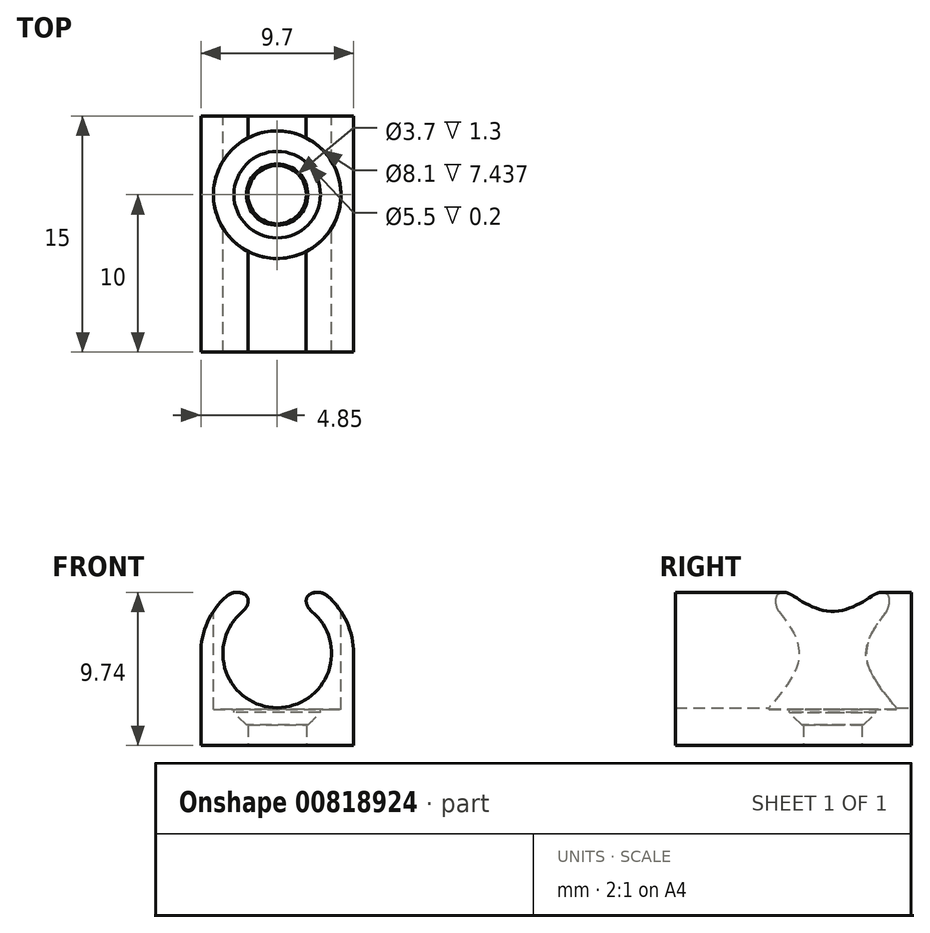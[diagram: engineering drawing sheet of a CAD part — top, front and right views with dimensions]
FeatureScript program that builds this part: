
annotation { "Feature Type Name" : "Feature", "Feature Type Description" : "" }
export const myFeature = defineFeature(function(context is Context, id is Id, definition is map)
    precondition{}
    {
        {
            var Q0;
            Q0=qCreatedBy(makeId("Front.planeOp"),FACE);
            var sketch = newSketch(context, id + "F0", { "sketchPlane" : qUnion([Q0])});
            skCircle(sketch, "E0", {"center": v(0, 0) * mm, "radius": 3.45 * mm});
            skArc(sketch, "E1.0", {"start": v(4.85, 0) * mm, "mid": v(0, 4.85) * mm, "end": v(-4.85, 0) * mm});
            skLineSegment(sketch, "E2", {"start": v(1.54, 3.09) * mm, "end": v(2.16, 4.34) * mm});
            skLineSegment(sketch, "E3.MirrorCS", {"start": v(-1.54, 3.09) * mm, "end": v(-2.16, 4.34) * mm});
            skLineSegment(sketch, "E4.bottom", {"start": v(-4.85, 0) * mm, "end": v(4.85, 0) * mm});
            skLineSegment(sketch, "E4.top", {"start": v(-4.85, -4.85) * mm, "end": v(4.85, -4.85) * mm});
            skLineSegment(sketch, "E4.left", {"start": v(-4.85, 0) * mm, "end": v(-4.85, -4.85) * mm});
            skLineSegment(sketch, "E4.right", {"start": v(4.85, 0) * mm, "end": v(4.85, -4.85) * mm});
            skLineSegment(sketch, "E5.0", {"start": v(-4.85, -5.85) * mm, "end": v(4.85, -5.85) * mm});
            skLineSegment(sketch, "E6", {"start": v(4.85, -5.85) * mm, "end": v(4.85, -4.85) * mm});
            skLineSegment(sketch, "E7", {"start": v(-4.85, -5.85) * mm, "end": v(-4.85, -4.85) * mm});
            skSolve(sketch);
        }
        {
            var Q0;
            Q0=makeQuery(id+"F0.imprint","IMPRINT",FACE,{"disambiguationData":[TD([[makeQuery(id+"F0.imprint","IMPRINT",EDGE,{"derivedFrom":sQuery(id+"F0.wireOp",EDGE,"E4.top")}),1.0]])]});
            var Q1;
            {var subQ0=sQuery(id+"F0.wireOp",EDGE,"E3.MirrorCS");Q1=makeQuery(id+"F0.imprint","IMPRINT",FACE,{"disambiguationData":[TD([[makeQuery(id+"F0.imprint","IMPRINT",EDGE,{"derivedFrom":subQ0}),1.0]])]});}
            var Q2;
            {var subQ0=sQuery(id+"F0.wireOp",EDGE,"E2");Q2=makeQuery(id+"F0.imprint","IMPRINT",FACE,{"disambiguationData":[TD([[makeQuery(id+"F0.imprint","IMPRINT",EDGE,{"derivedFrom":subQ0}),-1.0]])]});}
            var Q3;
            Q3=makeQuery(id+"F0.imprint","IMPRINT",FACE,{"disambiguationData":[TD([[makeQuery(id+"F0.imprint","IMPRINT",EDGE,{"derivedFrom":sQuery(id+"F0.wireOp",EDGE,"E4.top")}),-1.0]])]});
            extrude(context, id + "F1", {"entities" : qUnion([Q0, Q1, Q2, Q3]), "depth" : 15 * mm, "offsetDistance" : 25 * mm});
        }
        {
            var Q0;
            Q0=makeQuery(id+"F1.opExtrude","SWEPT_FACE",FACE,{"disambiguationData":[OSD([sQuery(id+"F0.wireOp",EDGE,"E5.0")])]});
            var sketch = newSketch(context, id + "F2", { "sketchPlane" : qUnion([Q0])});
            skLineSegment(sketch, "E8", {"start": v(0, 10) * mm, "end": v(0, 0) * mm, "construction": true});
            skPoint(sketch, "E9", {"position": v(0, 5) * mm});
            skCircle(sketch, "E10", {"center": v(0, 5) * mm, "radius": 1.85 * mm});
            skSolve(sketch);
        }
        {
            var Q0;
            Q0=makeQuery(id+"F2.imprint","IMPRINT",FACE,{"disambiguationData":[TD([[makeQuery(id+"F2.imprint","IMPRINT",EDGE,{"derivedFrom":sQuery(id+"F2.wireOp",EDGE,"E10")}),1.0]])]});
            extrude(context, id + "F3", {"entities" : qUnion([Q0]), "operationType" : NewBodyOperationType.REMOVE, "endBound" : BoundingType.THROUGH_ALL, "oppositeDirection" : true, "depth" : 25 * mm, "offsetDistance" : 25 * mm});
        }
        {
            var Q0;
            Q0=makeQuery(id+"F1.opExtrude","SWEPT_FACE",FACE,{"disambiguationData":[OSD([sQuery(id+"F0.wireOp",EDGE,"E5.0")])]});
            cPlane(context, id + "F4", {"entities" : qUnion([Q0]), "cplaneType" : CPlaneType.OFFSET, "offset" : 10.8 * mm, "oppositeDirection" : true, "width" : 150 * mm, "height" : 150 * mm});
        }
        {
            var Q0;
            Q0=qCreatedBy(id+"F4.planeOp",FACE);
            var sketch = newSketch(context, id + "F5", { "sketchPlane" : qUnion([Q0])});
            skLineSegment(sketch, "E11.0.0", {"start": v(-4.85, 0) * mm, "end": v(4.85, 0) * mm});
            skLineSegment(sketch, "E11.0.1", {"start": v(4.85, 0) * mm, "end": v(4.85, 15) * mm});
            skLineSegment(sketch, "E11.0.2", {"start": v(4.85, 15) * mm, "end": v(-4.85, 15) * mm});
            skLineSegment(sketch, "E11.0.3", {"start": v(-4.85, 15) * mm, "end": v(-4.85, 0) * mm});
            skCircle(sketch, "E12.0", {"center": v(0, 5) * mm, "radius": 1.85 * mm});
            skCircle(sketch, "E13", {"center": v(0, 5) * mm, "radius": 4.05 * mm});
            skSolve(sketch);
        }
        {
            var Q0;
            Q0=makeQuery(id+"F5.imprint","IMPRINT",FACE,{"disambiguationData":[TD([[makeQuery(id+"F5.imprint","IMPRINT",EDGE,{"derivedFrom":sQuery(id+"F5.wireOp",EDGE,"E12.0")}),-1.0]])]});
            var Q1;
            Q1=sQuery(id+"F5.wireOp",EDGE,"E13");
            extrude(context, id + "F6", {"entities" : qUnion([Q0]), "operationType" : NewBodyOperationType.REMOVE, "surfaceOperationType" : NewSurfaceOperationType.ADD, "surfaceEntities" : qUnion([Q1]), "depth" : 8.5 * mm, "offsetDistance" : 25 * mm});
        }
        {
            var Q0;
            Q0=makeQuery(id+"F6.boolean.opBoolean","COPY",FACE,{"derivedFrom":makeQuery(id+"F6.opExtrude","CAP_FACE",FACE,{"disambiguationData":[OSD([sQuery(id+"F5.wireOp",EDGE,"E12.0"),sQuery(id+"F5.wireOp",EDGE,"E13")])],"isStart":false})});
            var sketch = newSketch(context, id + "F7", { "sketchPlane" : qUnion([Q0])});
            skCircle(sketch, "E14.0", {"center": v(0, -5) * mm, "radius": 1.85 * mm});
            skCircle(sketch, "E15", {"center": v(0, -5) * mm, "radius": 2.75 * mm});
            skSolve(sketch);
        }
        {
            var Q0;
            Q0=makeQuery(id+"F7.imprint","IMPRINT",FACE,{"disambiguationData":[TD([[makeQuery(id+"F7.imprint","IMPRINT",EDGE,{"derivedFrom":sQuery(id+"F7.wireOp",EDGE,"E14.0")}),1.0]])]});
            extrude(context, id + "F8", {"entities" : qUnion([Q0]), "operationType" : NewBodyOperationType.REMOVE, "oppositeDirection" : true, "depth" : 1 * mm, "offsetDistance" : 25 * mm});
        }
        {
            var Q0;
            Q0=makeQuery(id+"F1.opExtrude","SWEPT_EDGE",EDGE,{"disambiguationData":[OSD([sQuery(id+"F0.wireOp",EDGE,"E1.0"),sQuery(id+"F0.wireOp",EDGE,"E3.MirrorCS")])]});
            var Q1;
            Q1=makeQuery(id+"F1.opExtrude","SWEPT_EDGE",EDGE,{"disambiguationData":[OSD([sQuery(id+"F0.wireOp",EDGE,"E0"),sQuery(id+"F0.wireOp",EDGE,"E3.MirrorCS")])]});
            var Q2;
            Q2=makeQuery(id+"F1.opExtrude","SWEPT_EDGE",EDGE,{"disambiguationData":[OSD([sQuery(id+"F0.wireOp",EDGE,"E1.0"),sQuery(id+"F0.wireOp",EDGE,"E2")])]});
            var Q3;
            Q3=makeQuery(id+"F1.opExtrude","SWEPT_EDGE",EDGE,{"disambiguationData":[OSD([sQuery(id+"F0.wireOp",EDGE,"E0"),sQuery(id+"F0.wireOp",EDGE,"E2")])]});
            fillet(context, id + "F9", {"entities" : qUnion([Q0, Q1, Q2, Q3]), "radius" : 1 * mm, "tangentPropagation" : true, "allowEdgeOverflow" : false});
        }
        {
            var Q0;
            {var subQ0=sQuery(id+"F0.wireOp",EDGE,"E3.MirrorCS");Q0=makeQuery(id+"F9.opFillet","BLEND_EDGE",EDGE,{"blendedFrom":[makeQuery(id+"F1.opExtrude","SWEPT_EDGE",EDGE,{"disambiguationData":[OSD([sQuery(id+"F0.wireOp",EDGE,"E0"),subQ0])]}),makeQuery(id+"F1.opExtrude","SWEPT_EDGE",EDGE,{"disambiguationData":[OSD([sQuery(id+"F0.wireOp",EDGE,"E1.0"),subQ0])]})],"blendedInto":[]});}
            var Q1;
            {var subQ0=sQuery(id+"F0.wireOp",EDGE,"E2");Q1=makeQuery(id+"F9.opFillet","BLEND_EDGE",EDGE,{"blendedFrom":[makeQuery(id+"F1.opExtrude","SWEPT_EDGE",EDGE,{"disambiguationData":[OSD([sQuery(id+"F0.wireOp",EDGE,"E0"),subQ0])]}),makeQuery(id+"F1.opExtrude","SWEPT_EDGE",EDGE,{"disambiguationData":[OSD([sQuery(id+"F0.wireOp",EDGE,"E1.0"),subQ0])]})],"blendedInto":[]});}
            fillet(context, id + "F10", {"entities" : qUnion([Q0, Q1]), "radius" : 0.5 * mm, "tangentPropagation" : true, "allowEdgeOverflow" : false});
        }
        {
            var Q0;
            Q0=makeQuery(id+"F8.boolean.opBoolean","COPY",EDGE,{"derivedFrom":makeQuery(id+"F8.opExtrude","CAP_EDGE",EDGE,{"disambiguationData":[OSD([sQuery(id+"F7.wireOp",EDGE,"E15")])],"isStart":false})});
            chamfer(context, id + "F11", {"entities" : qUnion([Q0]), "width" : 0.8 * mm, "tangentPropagation" : true});
        }
    });
